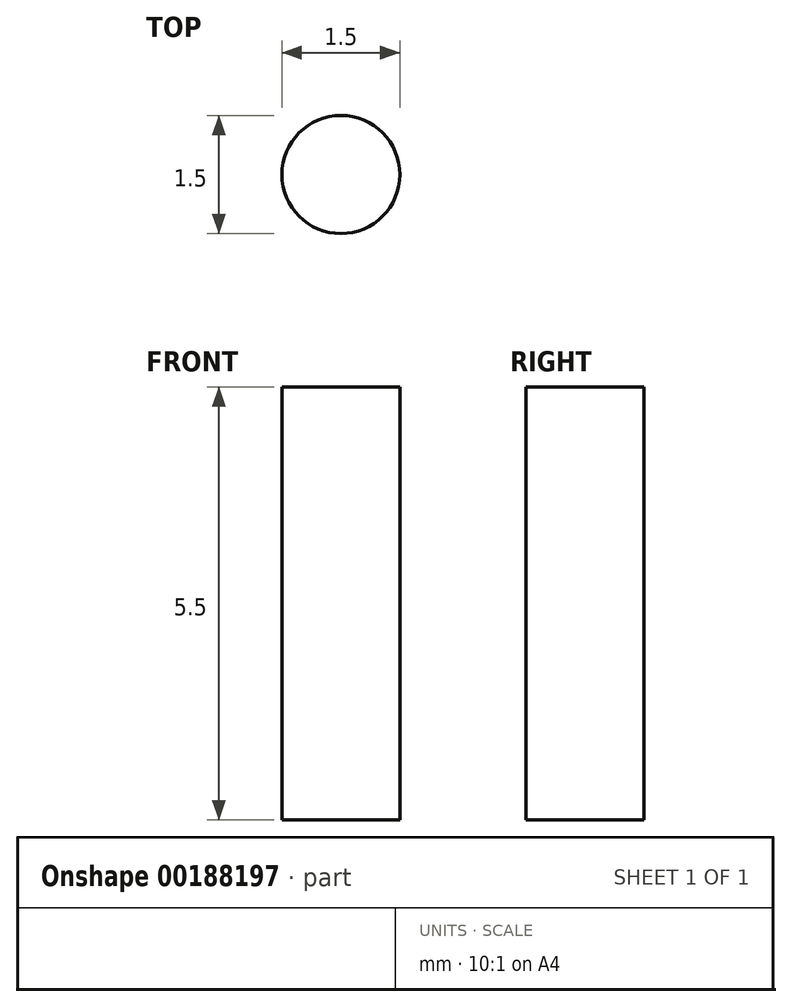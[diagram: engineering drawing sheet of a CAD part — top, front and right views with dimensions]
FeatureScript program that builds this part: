
annotation { "Feature Type Name" : "Feature", "Feature Type Description" : "" }
export const myFeature = defineFeature(function(context is Context, id is Id, definition is map)
    precondition{}
    {
        {
            var Q0;
            Q0=qCreatedBy(makeId("Top.planeOp"),FACE);
            var sketch = newSketch(context, id + "F0", { "sketchPlane" : qUnion([Q0])});
            skCircle(sketch, "E0", {"center": v(0, 0) * mm, "radius": 0.75 * mm});
            skSolve(sketch);
        }
        {
            var Q0;
            Q0=makeQuery(id+"F0.imprint","IMPRINT",FACE,{"disambiguationData":[TD([[makeQuery(id+"F0.imprint","IMPRINT",EDGE,{"derivedFrom":sQuery(id+"F0.wireOp",EDGE,"E0")}),1.0]])]});
            extrude(context, id + "F1", {"entities" : qUnion([Q0]), "depth" : 5.5 * mm});
        }
    });
